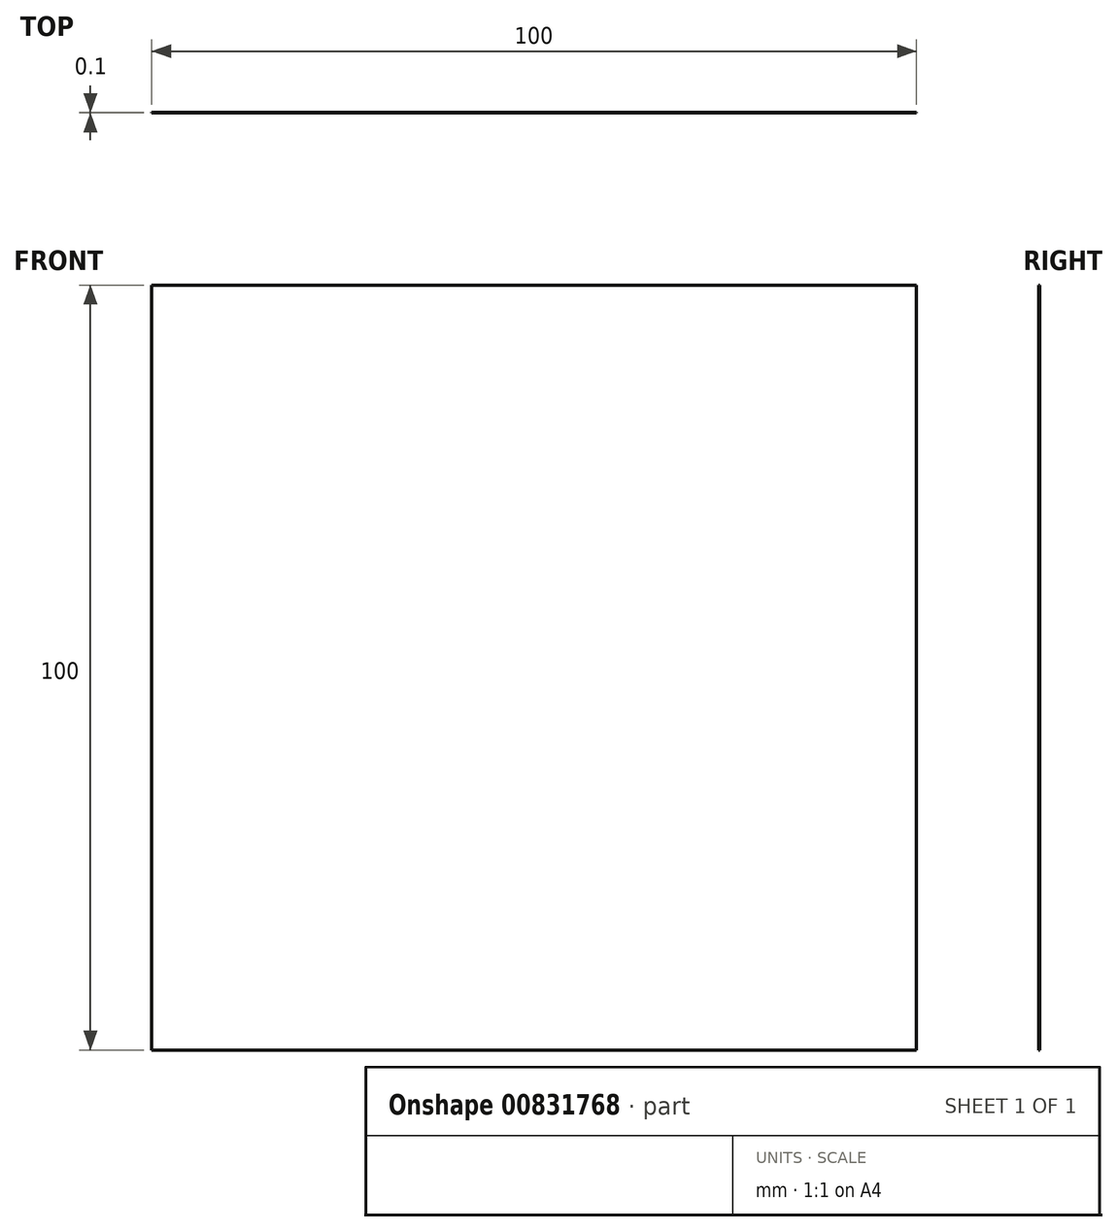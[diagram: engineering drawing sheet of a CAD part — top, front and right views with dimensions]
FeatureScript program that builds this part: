
annotation { "Feature Type Name" : "Feature", "Feature Type Description" : "" }
export const myFeature = defineFeature(function(context is Context, id is Id, definition is map)
    precondition{}
    {
        {
            var Q0;
            Q0=qCreatedBy(makeId("Front.planeOp"),FACE);
            var sketch = newSketch(context, id + "F0", { "sketchPlane" : qUnion([Q0])});
            skLineSegment(sketch, "E0.bottom", {"start": v(0, 0) * mm, "end": v(100, 0) * mm});
            skLineSegment(sketch, "E0.top", {"start": v(0, 100) * mm, "end": v(100, 100) * mm});
            skLineSegment(sketch, "E0.left", {"start": v(0, 0) * mm, "end": v(0, 100) * mm});
            skLineSegment(sketch, "E0.right", {"start": v(100, 0) * mm, "end": v(100, 100) * mm});
            skSolve(sketch);
        }
        {
            var Q0;
            Q0=makeQuery(id+"F0.imprint","IMPRINT",FACE,{"disambiguationData":[TD([[makeQuery(id+"F0.imprint","IMPRINT",EDGE,{"derivedFrom":sQuery(id+"F0.wireOp",EDGE,"E0.bottom")}),1.0]])]});
            extrude(context, id + "F1", {"entities" : qUnion([Q0]), "depth" : 0.1 * mm, "offsetDistance" : 25 * mm});
        }
    });
